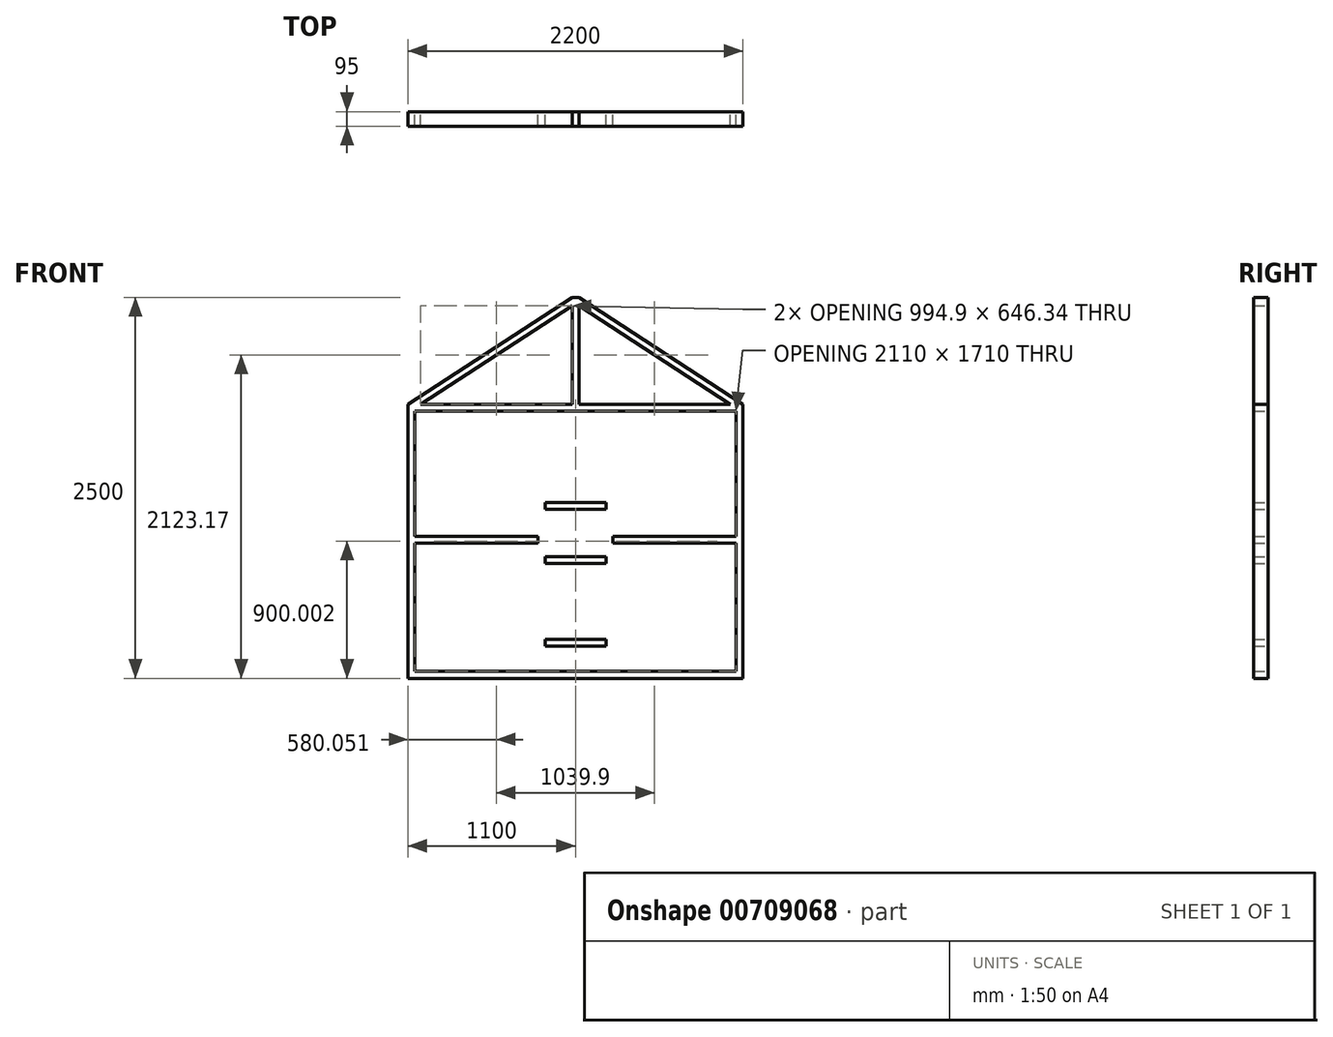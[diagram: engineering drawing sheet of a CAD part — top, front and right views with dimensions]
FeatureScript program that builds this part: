
annotation { "Feature Type Name" : "Feature", "Feature Type Description" : "" }
export const myFeature = defineFeature(function(context is Context, id is Id, definition is map)
    precondition{}
    {
        {
            var Q0;
            Q0=qCreatedBy(makeId("Front.planeOp"),FACE);
            var sketch = newSketch(context, id + "F0", { "sketchPlane" : qUnion([Q0])});
            skLineSegment(sketch, "E0.bottom", {"start": v(1100, -583.17) * mm, "end": v(-1100, -583.17) * mm});
            skLineSegment(sketch, "E0.top", {"start": v(1100, -628.17) * mm, "end": v(-1100, -628.17) * mm});
            skLineSegment(sketch, "E0.left", {"start": v(1100, -583.17) * mm, "end": v(1100, -628.17) * mm});
            skLineSegment(sketch, "E0.right", {"start": v(-1100, -583.17) * mm, "end": v(-1100, -628.17) * mm});
            skPoint(sketch, "E0.middle", {"position": v(0, -605.67) * mm});
            skLineSegment(sketch, "E1.bottom", {"start": v(1100, 1171.83) * mm, "end": v(-1100, 1171.83) * mm});
            skLineSegment(sketch, "E1.top", {"start": v(1100, 1126.83) * mm, "end": v(-1100, 1126.83) * mm});
            skLineSegment(sketch, "E1.left", {"start": v(1100, 1171.83) * mm, "end": v(1100, 1126.83) * mm});
            skLineSegment(sketch, "E1.right", {"start": v(-1100, 1171.83) * mm, "end": v(-1100, 1126.83) * mm});
            skPoint(sketch, "E1.middle", {"position": v(0, 1149.33) * mm});
            skLineSegment(sketch, "E2.bottom", {"start": v(1100, 1126.83) * mm, "end": v(1055, 1126.83) * mm});
            skLineSegment(sketch, "E2.top", {"start": v(1100, -583.17) * mm, "end": v(1055, -583.17) * mm});
            skLineSegment(sketch, "E2.left", {"start": v(1100, 1126.83) * mm, "end": v(1100, -583.17) * mm});
            skLineSegment(sketch, "E2.right", {"start": v(1055, 1126.83) * mm, "end": v(1055, -583.17) * mm});
            skLineSegment(sketch, "E3.bottom", {"start": v(-1100, 1126.83) * mm, "end": v(-1055, 1126.83) * mm});
            skLineSegment(sketch, "E3.top", {"start": v(-1100, -583.17) * mm, "end": v(-1055, -583.17) * mm});
            skLineSegment(sketch, "E3.left", {"start": v(-1100, 1126.83) * mm, "end": v(-1100, -583.17) * mm});
            skLineSegment(sketch, "E3.right", {"start": v(-1055, 1126.83) * mm, "end": v(-1055, -583.17) * mm});
            skLineSegment(sketch, "E4.bottom", {"start": v(-245, -583.17) * mm, "end": v(-200, -583.17) * mm});
            skLineSegment(sketch, "E4.top", {"start": v(-245, 1126.83) * mm, "end": v(-200, 1126.83) * mm});
            skLineSegment(sketch, "E4.left", {"start": v(-245, -583.17) * mm, "end": v(-245, 1126.83) * mm});
            skLineSegment(sketch, "E4.right", {"start": v(-200, -583.17) * mm, "end": v(-200, 1126.83) * mm});
            skLineSegment(sketch, "E5.bottom", {"start": v(200, 1126.83) * mm, "end": v(245, 1126.83) * mm});
            skLineSegment(sketch, "E5.top", {"start": v(200, -583.17) * mm, "end": v(245, -583.17) * mm});
            skLineSegment(sketch, "E5.left", {"start": v(245, 1126.83) * mm, "end": v(245, -583.17) * mm});
            skLineSegment(sketch, "E5.right", {"start": v(200, 1126.83) * mm, "end": v(200, -583.17) * mm});
            skLineSegment(sketch, "E6.bottom", {"start": v(-200, -373.17) * mm, "end": v(200, -373.17) * mm});
            skLineSegment(sketch, "E6.top", {"start": v(-200, -418.17) * mm, "end": v(200, -418.17) * mm});
            skLineSegment(sketch, "E6.left", {"start": v(-200, -373.17) * mm, "end": v(-200, -418.17) * mm});
            skLineSegment(sketch, "E6.right", {"start": v(200, -373.17) * mm, "end": v(200, -418.17) * mm});
            skLineSegment(sketch, "E7", {"start": v(-1055, 259.83) * mm, "end": v(-245, 259.83) * mm});
            skLineSegment(sketch, "E8", {"start": v(-1055, 304.83) * mm, "end": v(-245, 304.83) * mm});
            skLineSegment(sketch, "E9.bottom", {"start": v(-22.5, 1171.83) * mm, "end": v(22.5, 1171.83) * mm});
            skLineSegment(sketch, "E9.top", {"start": v(-22.5, 1871.83) * mm, "end": v(22.5, 1871.83) * mm});
            skLineSegment(sketch, "E9.left", {"start": v(-22.5, 1171.83) * mm, "end": v(-22.5, 1871.83) * mm});
            skLineSegment(sketch, "E9.right", {"start": v(22.5, 1171.83) * mm, "end": v(22.5, 1871.83) * mm});
            skLineSegment(sketch, "E10", {"start": v(-1100, 1171.83) * mm, "end": v(-22.5, 1871.83) * mm});
            skLineSegment(sketch, "E11", {"start": v(22.5, 1871.83) * mm, "end": v(1100, 1171.83) * mm});
            skLineSegment(sketch, "E12", {"start": v(-1017.4, 1171.83) * mm, "end": v(-22.5, 1818.17) * mm});
            skLineSegment(sketch, "E13", {"start": v(22.5, 1818.17) * mm, "end": v(1017.4, 1171.83) * mm});
            skLineSegment(sketch, "E14", {"start": v(245, 304.83) * mm, "end": v(1055, 304.83) * mm});
            skLineSegment(sketch, "E15", {"start": v(1055, 259.83) * mm, "end": v(245, 259.83) * mm});
            skPoint(sketch, "E15.endSnap0", {"position": v(245, 271.83) * mm});
            skLineSegment(sketch, "E16", {"start": v(-200, 126.83) * mm, "end": v(200, 126.83) * mm});
            skLineSegment(sketch, "E17", {"start": v(-200, 171.83) * mm, "end": v(200, 171.83) * mm});
            skLineSegment(sketch, "E18", {"start": v(-200, 526.83) * mm, "end": v(200, 526.83) * mm});
            skLineSegment(sketch, "E19", {"start": v(-200, 481.83) * mm, "end": v(200, 481.83) * mm});
            skSolve(sketch);
        }
        {
            var Q0;
            Q0=qSketchRegion(id+"F0",true);
            var Q1;
            {var subQ0=sQuery(id+"F0.wireOp",EDGE,"apKnzXqb-7Lmc-cgBK-WmSE-JRUgLc3Nn7XE");Q1=makeQuery(id+"F0.imprint","IMPRINT",FACE,{"disambiguationData":[TD([[makeQuery(id+"F0.imprint","IMPRINT",EDGE,{"derivedFrom":subQ0}),1.0]])]});}
            var Q2;
            {var subQ3=sQuery(id+"F0.wireOp",EDGE,"E4.bottom");Q2=makeQuery(id+"F0.imprint","IMPRINT",FACE,{"disambiguationData":[TD([[makeQuery(id+"F0.imprint","IMPRINT",EDGE,{"derivedFrom":subQ3}),1.0]])]});}
            var Q3;
            {var subQ3=sQuery(id+"F0.wireOp",EDGE,"E5.bottom");Q3=makeQuery(id+"F0.imprint","IMPRINT",FACE,{"disambiguationData":[TD([[makeQuery(id+"F0.imprint","IMPRINT",EDGE,{"derivedFrom":subQ3}),-1.0]])]});}
            var Q4;
            {var subQ0=sQuery(id+"F0.wireOp",EDGE,"8ff269b6-e355-413f-98f4-d15c09b805400.MirrorCS");Q4=makeQuery(id+"F0.imprint","IMPRINT",FACE,{"disambiguationData":[TD([[makeQuery(id+"F0.imprint","IMPRINT",EDGE,{"derivedFrom":subQ0}),-1.0]])]});}
            var Q5;
            {var subQ0=sQuery(id+"F0.wireOp",EDGE,"E7");Q5=makeQuery(id+"F0.imprint","IMPRINT",FACE,{"disambiguationData":[TD([[makeQuery(id+"F0.imprint","IMPRINT",EDGE,{"derivedFrom":subQ0}),1.0]])]});}
            var Q6;
            Q6=makeQuery(id+"F0.imprint","IMPRINT",FACE,{"disambiguationData":[TD([[makeQuery(id+"F0.imprint","IMPRINT",EDGE,{"derivedFrom":sQuery(id+"F0.wireOp",EDGE,"E6.bottom")}),-1.0]])]});
            var Q7;
            {var subQ0=sQuery(id+"F0.wireOp",EDGE,"E16");Q7=makeQuery(id+"F0.imprint","IMPRINT",FACE,{"disambiguationData":[TD([[makeQuery(id+"F0.imprint","IMPRINT",EDGE,{"derivedFrom":subQ0}),1.0]])]});}
            var Q8;
            {var subQ0=sQuery(id+"F0.wireOp",EDGE,"E14");Q8=makeQuery(id+"F0.imprint","IMPRINT",FACE,{"disambiguationData":[TD([[makeQuery(id+"F0.imprint","IMPRINT",EDGE,{"derivedFrom":subQ0}),-1.0]])]});}
            var Q9;
            {var subQ0=sQuery(id+"F0.wireOp",EDGE,"E18");Q9=makeQuery(id+"F0.imprint","IMPRINT",FACE,{"disambiguationData":[TD([[makeQuery(id+"F0.imprint","IMPRINT",EDGE,{"derivedFrom":subQ0}),-1.0]])]});}
            extrude(context, id + "F1", {"entities" : qUnion([Q0, Q1, Q2, Q3, Q4, Q5, Q6, Q7, Q8, Q9]), "depth" : 95 * mm, "offsetDistance" : 25 * mm});
        }
    });
